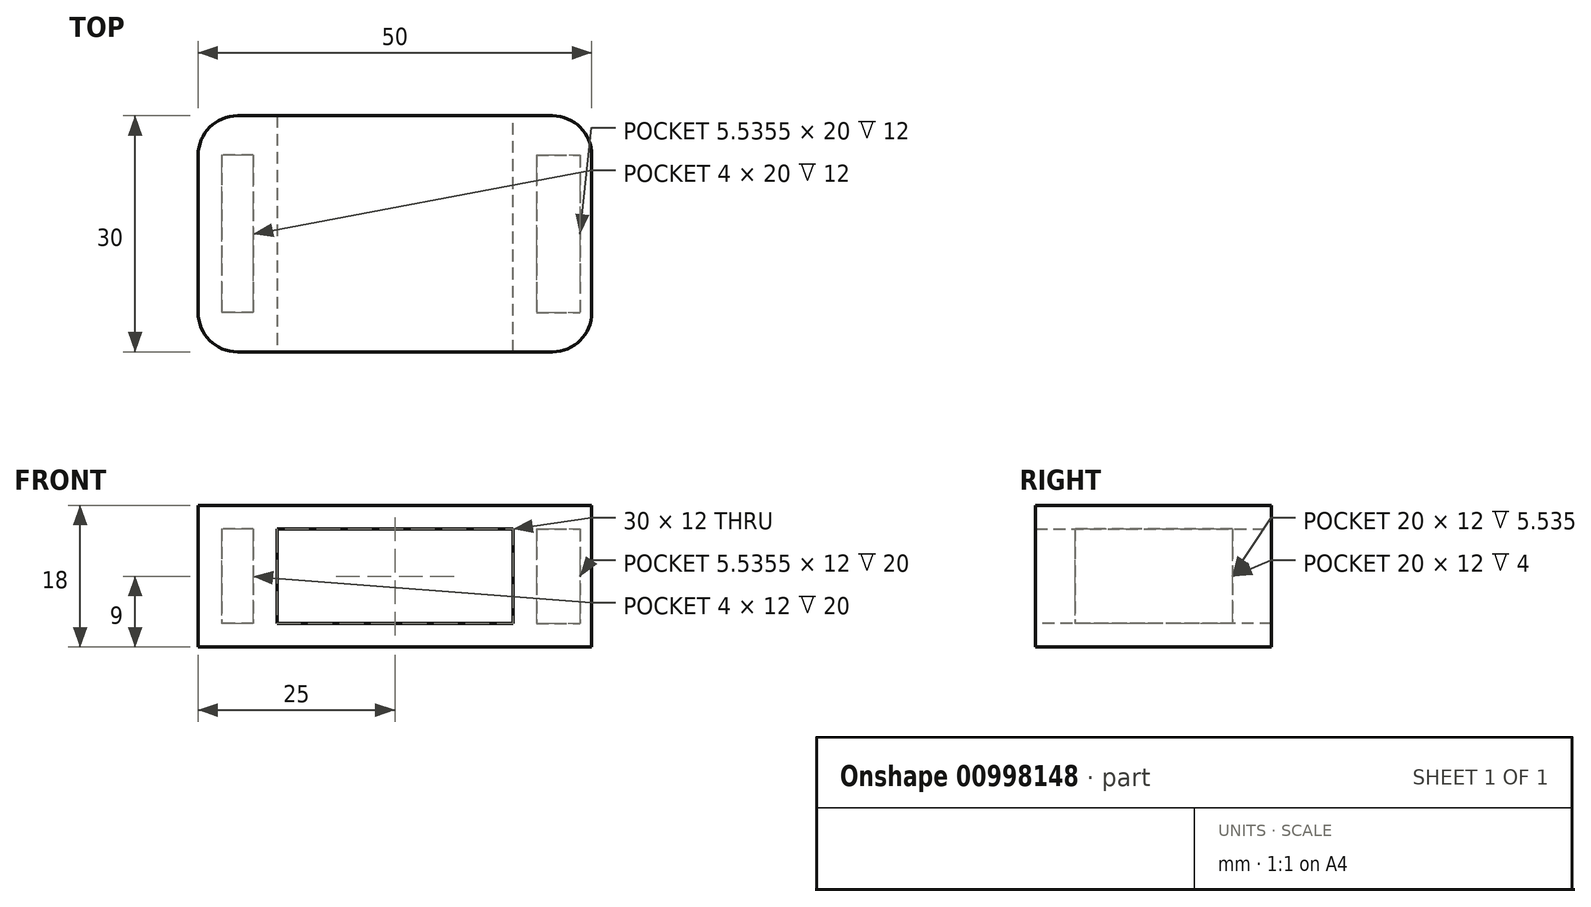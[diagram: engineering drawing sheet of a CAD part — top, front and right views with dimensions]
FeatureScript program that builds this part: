
annotation { "Feature Type Name" : "Feature", "Feature Type Description" : "" }
export const myFeature = defineFeature(function(context is Context, id is Id, definition is map)
    precondition{}
    {
        {
            var Q0;
            Q0=qCreatedBy(makeId("Top.planeOp"),FACE);
            var sketch = newSketch(context, id + "F0", { "sketchPlane" : qUnion([Q0])});
            skLineSegment(sketch, "E0.bottom", {"start": v(-5, 0) * mm, "end": v(-45, 0) * mm});
            skLineSegment(sketch, "E0.top", {"start": v(-5, 30) * mm, "end": v(-45, 30) * mm});
            skLineSegment(sketch, "E0.left", {"start": v(0, 5) * mm, "end": v(0, 25) * mm});
            skLineSegment(sketch, "E0.right", {"start": v(-50, 5) * mm, "end": v(-50, 25) * mm});
            skPoint(sketch, "E1.visualSharp", {"position": v(-50, 30) * mm});
            skArc(sketch, "E1.filletArc", {"start": v(-45, 30) * mm, "mid": v(-48.54, 28.54) * mm, "end": v(-50, 25) * mm});
            skPoint(sketch, "E2.visualSharp", {"position": v(0, 30) * mm});
            skArc(sketch, "E2.filletArc", {"start": v(0, 25) * mm, "mid": v(-1.46, 28.54) * mm, "end": v(-5, 30) * mm});
            skPoint(sketch, "E3.visualSharp", {"position": v(0, 0) * mm});
            skArc(sketch, "E3.filletArc", {"start": v(-5, 0) * mm, "mid": v(-1.46, 1.46) * mm, "end": v(0, 5) * mm});
            skPoint(sketch, "E4.visualSharp", {"position": v(-50, 0) * mm});
            skArc(sketch, "E4.filletArc", {"start": v(-50, 5) * mm, "mid": v(-48.54, 1.46) * mm, "end": v(-45, 0) * mm});
            skSolve(sketch);
        }
        {
            var Q0;
            Q0=makeQuery(id+"F0.imprint","IMPRINT",FACE,{"disambiguationData":[TD([[makeQuery(id+"F0.imprint","IMPRINT",EDGE,{"derivedFrom":sQuery(id+"F0.wireOp",EDGE,"E0.bottom")}),-1.0]])]});
            extrude(context, id + "F1", {"entities" : qUnion([Q0]), "depth" : 3 * mm, "offsetDistance" : 25 * mm});
        }
        {
            var Q0;
            Q0=makeQuery(id+"F1.opExtrude","CAP_FACE",FACE,{"disambiguationData":[OSD([sQuery(id+"F0.wireOp",EDGE,"E0.bottom"),sQuery(id+"F0.wireOp",EDGE,"E0.top"),sQuery(id+"F0.wireOp",EDGE,"E0.left"),sQuery(id+"F0.wireOp",EDGE,"E0.right"),sQuery(id+"F0.wireOp",EDGE,"E1.filletArc"),sQuery(id+"F0.wireOp",EDGE,"E2.filletArc"),sQuery(id+"F0.wireOp",EDGE,"E3.filletArc"),sQuery(id+"F0.wireOp",EDGE,"E4.filletArc")])],"isStart":false});
            var sketch = newSketch(context, id + "F2", { "sketchPlane" : qUnion([Q0])});
            skLineSegment(sketch, "E5.bottom", {"start": v(-5, 0) * mm, "end": v(-10, 0) * mm});
            skLineSegment(sketch, "E5.top", {"start": v(-5, 30) * mm, "end": v(-10, 30) * mm});
            skLineSegment(sketch, "E5.left", {"start": v(0, 5) * mm, "end": v(0, 25) * mm});
            skLineSegment(sketch, "E5.right", {"start": v(-10, 0) * mm, "end": v(-10, 30) * mm});
            skLineSegment(sketch, "E6.bottom", {"start": v(-45, 30) * mm, "end": v(-40, 30) * mm});
            skLineSegment(sketch, "E6.top", {"start": v(-45, 0) * mm, "end": v(-40, 0) * mm});
            skLineSegment(sketch, "E6.left", {"start": v(-50, 25) * mm, "end": v(-50, 5) * mm});
            skLineSegment(sketch, "E6.right", {"start": v(-40, 30) * mm, "end": v(-40, 0) * mm});
            skPoint(sketch, "E7.visualSharp", {"position": v(-50, 30) * mm});
            skArc(sketch, "E7.filletArc", {"start": v(-45, 30) * mm, "mid": v(-48.54, 28.54) * mm, "end": v(-50, 25) * mm});
            skPoint(sketch, "E8.visualSharp", {"position": v(-50, 0) * mm});
            skArc(sketch, "E8.filletArc", {"start": v(-50, 5) * mm, "mid": v(-48.54, 1.46) * mm, "end": v(-45, 0) * mm});
            skPoint(sketch, "E9.visualSharp", {"position": v(0, 0) * mm});
            skArc(sketch, "E9.filletArc", {"start": v(-5, 0) * mm, "mid": v(-1.46, 1.46) * mm, "end": v(0, 5) * mm});
            skPoint(sketch, "E10.visualSharp", {"position": v(0, 30) * mm});
            skArc(sketch, "E10.filletArc", {"start": v(0, 25) * mm, "mid": v(-1.46, 28.54) * mm, "end": v(-5, 30) * mm});
            skLineSegment(sketch, "E11.bottom", {"start": v(-43, 25) * mm, "end": v(-47, 25) * mm});
            skLineSegment(sketch, "E11.top", {"start": v(-43, 5) * mm, "end": v(-47, 5) * mm});
            skLineSegment(sketch, "E11.left", {"start": v(-43, 25) * mm, "end": v(-43, 5) * mm});
            skLineSegment(sketch, "E11.right", {"start": v(-47, 25) * mm, "end": v(-47, 5) * mm});
            skPoint(sketch, "E12.oppositeSnap0", {"position": v(-1.46, 1.46) * mm});
            skLineSegment(sketch, "E12.bottom", {"start": v(-7, 25) * mm, "end": v(-1.46, 25) * mm});
            skLineSegment(sketch, "E12.top", {"start": v(-7, 5) * mm, "end": v(-1.46, 5) * mm});
            skLineSegment(sketch, "E12.left", {"start": v(-7, 25) * mm, "end": v(-7, 5) * mm});
            skLineSegment(sketch, "E12.right", {"start": v(-1.46, 25) * mm, "end": v(-1.46, 5) * mm});
            skSolve(sketch);
        }
        {
            var Q0;
            Q0=makeQuery(id+"F2.imprint","IMPRINT",FACE,{"disambiguationData":[TD([[makeQuery(id+"F2.imprint","IMPRINT",EDGE,{"derivedFrom":sQuery(id+"F2.wireOp",EDGE,"E6.bottom")}),1.0]])]});
            var Q1;
            Q1=makeQuery(id+"F2.imprint","IMPRINT",FACE,{"disambiguationData":[TD([[makeQuery(id+"F2.imprint","IMPRINT",EDGE,{"derivedFrom":sQuery(id+"F2.wireOp",EDGE,"E5.bottom")}),-1.0]])]});
            extrude(context, id + "F3", {"entities" : qUnion([Q0, Q1]), "operationType" : NewBodyOperationType.ADD, "depth" : 7 * mm, "offsetDistance" : 25 * mm});
        }
        {
            var Q0;
            Q0=makeQuery(id+"F3.opExtrude","CAP_FACE",FACE,{"disambiguationData":[OSD([sQuery(id+"F2.wireOp",EDGE,"E6.bottom"),sQuery(id+"F2.wireOp",EDGE,"E6.top"),sQuery(id+"F2.wireOp",EDGE,"E6.left"),sQuery(id+"F2.wireOp",EDGE,"E6.right"),sQuery(id+"F2.wireOp",EDGE,"E7.filletArc"),sQuery(id+"F2.wireOp",EDGE,"E8.filletArc"),sQuery(id+"F2.wireOp",EDGE,"E11.bottom"),sQuery(id+"F2.wireOp",EDGE,"E11.top"),sQuery(id+"F2.wireOp",EDGE,"E11.left"),sQuery(id+"F2.wireOp",EDGE,"E11.right")])],"isStart":false});
            var Q1;
            Q1=makeQuery(id+"F3.opExtrude","CAP_FACE",FACE,{"disambiguationData":[OSD([sQuery(id+"F2.wireOp",EDGE,"E5.bottom"),sQuery(id+"F2.wireOp",EDGE,"E5.top"),sQuery(id+"F2.wireOp",EDGE,"E5.left"),sQuery(id+"F2.wireOp",EDGE,"E5.right"),sQuery(id+"F2.wireOp",EDGE,"E9.filletArc"),sQuery(id+"F2.wireOp",EDGE,"E10.filletArc"),sQuery(id+"F2.wireOp",EDGE,"E12.bottom"),sQuery(id+"F2.wireOp",EDGE,"E12.top"),sQuery(id+"F2.wireOp",EDGE,"E12.left"),sQuery(id+"F2.wireOp",EDGE,"E12.right")])],"isStart":false});
            extrude(context, id + "F4", {"entities" : qUnion([Q0, Q1]), "operationType" : NewBodyOperationType.ADD, "depth" : 5 * mm, "offsetDistance" : 25 * mm});
        }
        {
            var Q0;
            Q0=makeQuery(id+"F4.opExtrude","CAP_FACE",FACE,{"disambiguationData":[OSD([sQuery(id+"F2.wireOp",EDGE,"E6.bottom"),sQuery(id+"F2.wireOp",EDGE,"E6.top"),sQuery(id+"F2.wireOp",EDGE,"E6.left"),sQuery(id+"F2.wireOp",EDGE,"E6.right"),sQuery(id+"F2.wireOp",EDGE,"E7.filletArc"),sQuery(id+"F2.wireOp",EDGE,"E8.filletArc"),sQuery(id+"F2.wireOp",EDGE,"E11.bottom"),sQuery(id+"F2.wireOp",EDGE,"E11.top"),sQuery(id+"F2.wireOp",EDGE,"E11.left"),sQuery(id+"F2.wireOp",EDGE,"E11.right")])],"isStart":false});
            var sketch = newSketch(context, id + "F5", { "sketchPlane" : qUnion([Q0])});
            skLineSegment(sketch, "E13.bottom", {"start": v(-5, 0) * mm, "end": v(-45, 0) * mm});
            skLineSegment(sketch, "E13.top", {"start": v(-5, 30) * mm, "end": v(-45, 30) * mm});
            skLineSegment(sketch, "E13.left", {"start": v(0, 5) * mm, "end": v(0, 25) * mm});
            skLineSegment(sketch, "E13.right", {"start": v(-50, 5) * mm, "end": v(-50, 25) * mm});
            skPoint(sketch, "E14.visualSharp", {"position": v(-50, 30) * mm});
            skArc(sketch, "E14.filletArc", {"start": v(-45, 30) * mm, "mid": v(-48.54, 28.54) * mm, "end": v(-50, 25) * mm});
            skPoint(sketch, "E15.visualSharp", {"position": v(0, 30) * mm});
            skArc(sketch, "E15.filletArc", {"start": v(0, 25) * mm, "mid": v(-1.46, 28.54) * mm, "end": v(-5, 30) * mm});
            skPoint(sketch, "E16.visualSharp", {"position": v(0, 0) * mm});
            skArc(sketch, "E16.filletArc", {"start": v(-5, 0) * mm, "mid": v(-1.46, 1.46) * mm, "end": v(0, 5) * mm});
            skPoint(sketch, "E17.visualSharp", {"position": v(-50, 0) * mm});
            skArc(sketch, "E17.filletArc", {"start": v(-50, 5) * mm, "mid": v(-48.54, 1.46) * mm, "end": v(-45, 0) * mm});
            skSolve(sketch);
        }
        {
            var Q0;
            Q0=makeQuery(id+"F5.imprint","IMPRINT",FACE,{"disambiguationData":[TD([[makeQuery(id+"F5.imprint","IMPRINT",EDGE,{"derivedFrom":sQuery(id+"F5.wireOp",EDGE,"E13.right")}),-1.0]])]});
            var Q1;
            Q1=makeQuery(id+"F5.imprint","IMPRINT",FACE,{"disambiguationData":[TD([[makeQuery(id+"F5.imprint","IMPRINT",EDGE,{"derivedFrom":sQuery(id+"F5.wireOp",EDGE,"E13.left")}),1.0]])]});
            var Q2;
            Q2=makeQuery(id+"F5.imprint","IMPRINT",FACE,{"disambiguationData":[TD([[makeQuery(id+"F5.imprint","IMPRINT",EDGE,{"derivedFrom":makeQuery(id+"F4.opExtrude","CAP_EDGE",EDGE,{"disambiguationData":[OSD([sQuery(id+"F2.wireOp",EDGE,"E11.bottom")])],"isStart":false})}),1.0]])]});
            extrude(context, id + "F6", {"entities" : qUnion([Q0, Q1, Q2]), "operationType" : NewBodyOperationType.ADD, "depth" : 3 * mm, "offsetDistance" : 25 * mm});
        }
    });
